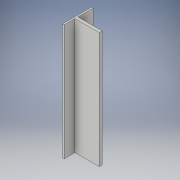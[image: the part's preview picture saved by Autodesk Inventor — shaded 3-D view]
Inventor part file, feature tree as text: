
AUTODESK INVENTOR PART (.ipt)
format: ipt  version: 2019 (Build 230136000, 136)  size: 115,200 bytes
history: native  units: in
note: dims shown in document units (in); Inventor stores cm internally (conversion verified against a paired STEP export)
features: extrude x2, sketch x2
ambient origin geometry x8: Origin, YZ Plane, XZ Plane, XY Plane, X Axis, Y Axis, Z Axis, Center Point
bodies: Solid1 (feature_tree)
feature tree (4):
  extrude  "Extrusion1"  Depth=9.0in
  extrude  "Extrusion2"  Depth=9.0in
  sketch  "Sketch1"  dims[d0=0.126in d1=9.0in]
  sketch  "Sketch2"  dims[d2=2.26in d3=0.0in d4=9.0in d5=0.222in d6=0.844in d7=1.885in d8=0.0in]
